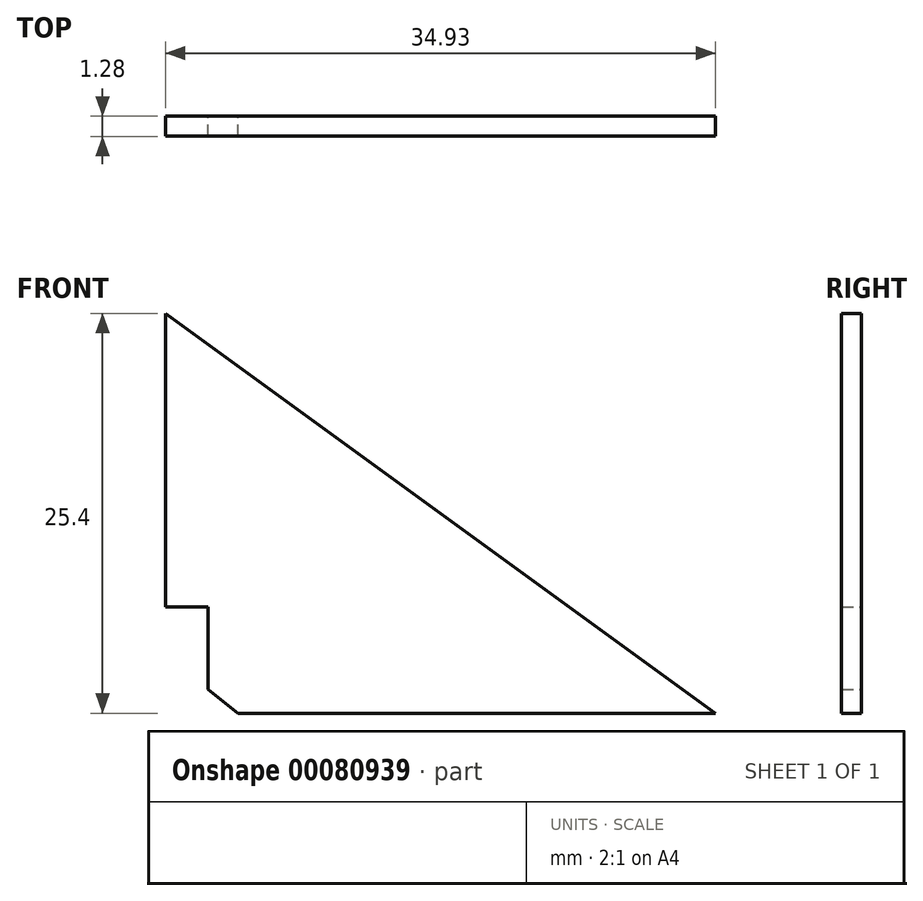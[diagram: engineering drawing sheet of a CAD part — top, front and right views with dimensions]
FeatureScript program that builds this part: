
annotation { "Feature Type Name" : "Feature", "Feature Type Description" : "" }
export const myFeature = defineFeature(function(context is Context, id is Id, definition is map)
    precondition{}
    {
        {
            var Q0;
            Q0=qCreatedBy(makeId("Front.planeOp"),FACE);
            var sketch = newSketch(context, id + "F0", { "sketchPlane" : qUnion([Q0])});
            skLineSegment(sketch, "E0", {"start": v(0, 6.77) * mm, "end": v(0, 25.4) * mm});
            skLineSegment(sketch, "E1", {"start": v(0, 25.4) * mm, "end": v(34.93, 0) * mm});
            skLineSegment(sketch, "E2", {"start": v(34.93, 0) * mm, "end": v(4.62, 0) * mm});
            skLineSegment(sketch, "E3", {"start": v(4.62, 0) * mm, "end": v(2.72, 1.5) * mm});
            skLineSegment(sketch, "E4", {"start": v(2.72, 1.5) * mm, "end": v(2.72, 6.77) * mm});
            skLineSegment(sketch, "E5", {"start": v(2.72, 6.77) * mm, "end": v(0, 6.77) * mm});
            skSolve(sketch);
        }
        {
            var Q0;
            Q0=makeQuery(id+"F0.imprint","IMPRINT",FACE,{"disambiguationData":[TD([[makeQuery(id+"F0.imprint","IMPRINT",EDGE,{"derivedFrom":sQuery(id+"F0.wireOp",EDGE,"E0")}),-1.0]])]});
            extrude(context, id + "F1", {"entities" : qUnion([Q0]), "depth" : 1.27 * mm, "symmetric" : true});
        }
    });
